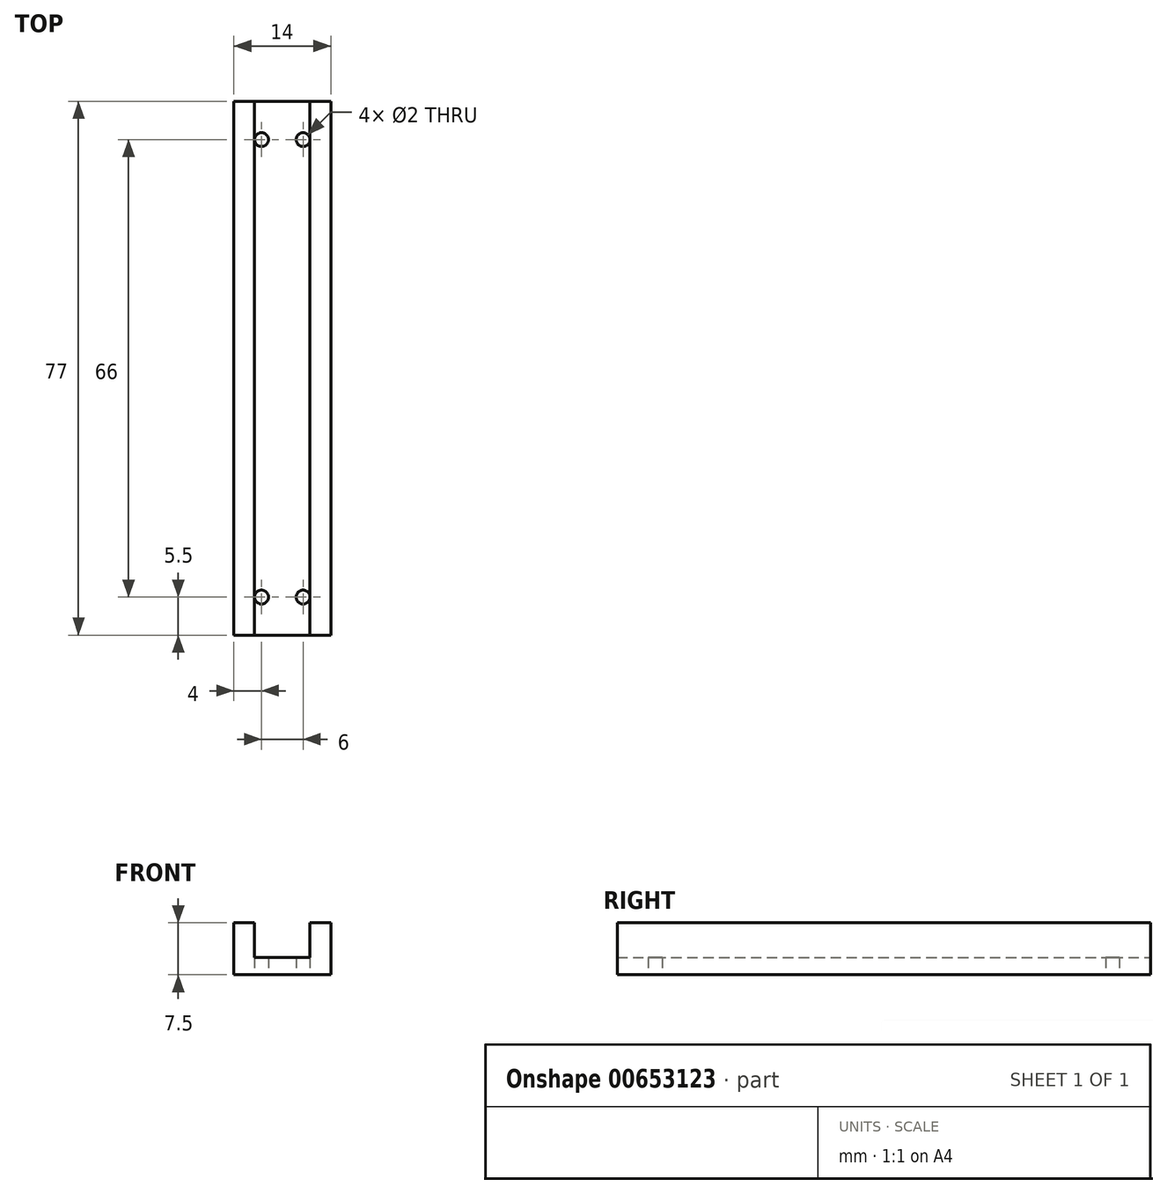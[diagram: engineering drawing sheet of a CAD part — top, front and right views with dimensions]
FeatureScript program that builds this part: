
annotation { "Feature Type Name" : "Feature", "Feature Type Description" : "" }
export const myFeature = defineFeature(function(context is Context, id is Id, definition is map)
    precondition{}
    {
        {
            var Q0;
            Q0=qCreatedBy(makeId("Front.planeOp"),FACE);
            var sketch = newSketch(context, id + "F0", { "sketchPlane" : qUnion([Q0])});
            skLineSegment(sketch, "E0", {"start": v(0, 7.5) * mm, "end": v(0, 0) * mm});
            skLineSegment(sketch, "E1", {"start": v(0, 0) * mm, "end": v(14, 0) * mm});
            skLineSegment(sketch, "E2", {"start": v(14, 0) * mm, "end": v(14, 7.5) * mm});
            skLineSegment(sketch, "E3", {"start": v(0, 7.5) * mm, "end": v(3, 7.5) * mm});
            skLineSegment(sketch, "E4", {"start": v(3, 7.5) * mm, "end": v(3, 2.5) * mm});
            skLineSegment(sketch, "E5", {"start": v(3, 2.5) * mm, "end": v(11, 2.5) * mm});
            skLineSegment(sketch, "E6", {"start": v(11, 2.5) * mm, "end": v(11, 7.5) * mm});
            skLineSegment(sketch, "E7", {"start": v(11, 7.5) * mm, "end": v(14, 7.5) * mm});
            skSolve(sketch);
        }
        {
            var Q0;
            Q0 = qSketchRegion(id + "F0", true);
            extrude(context, id + "F1", {"entities" : qUnion([Q0]), "depth" : 77 * mm, "offsetDistance" : 25 * mm});
        }
        {
            var Q0;
            Q0=makeQuery(id+"F1.opExtrude","SWEPT_FACE",FACE,{"disambiguationData":[OSD([sQuery(id+"F0.wireOp",EDGE,"E1")])]});
            var sketch = newSketch(context, id + "F2", { "sketchPlane" : qUnion([Q0])});
            skLineSegment(sketch, "E8", {"start": v(7, -23.91) * mm, "end": v(7, 98.97) * mm, "construction": true});
            skLineSegment(sketch, "E9", {"start": v(55.18, 38.5) * mm, "end": v(-55.25, 38.5) * mm, "construction": true});
            skLineSegment(sketch, "E10", {"start": v(36.92, 5.5) * mm, "end": v(-29.68, 5.5) * mm, "construction": true});
            skLineSegment(sketch, "E11", {"start": v(38.32, 71.5) * mm, "end": v(-31.37, 71.5) * mm, "construction": true});
            skCircle(sketch, "E12", {"center": v(10, 5.5) * mm, "radius": 1 * mm});
            skCircle(sketch, "E13", {"center": v(4, 5.5) * mm, "radius": 1 * mm});
            skCircle(sketch, "E14", {"center": v(10, 71.5) * mm, "radius": 1 * mm});
            skCircle(sketch, "E15", {"center": v(4, 71.5) * mm, "radius": 1 * mm});
            skSolve(sketch);
        }
        {
            var Q0;
            Q0 = qSketchRegion(id + "F2", true);
            extrude(context, id + "F3", {"entities" : qUnion([Q0]), "operationType" : NewBodyOperationType.REMOVE, "oppositeDirection" : true, "depth" : 25 * mm, "offsetDistance" : 25 * mm});
        }
    });
